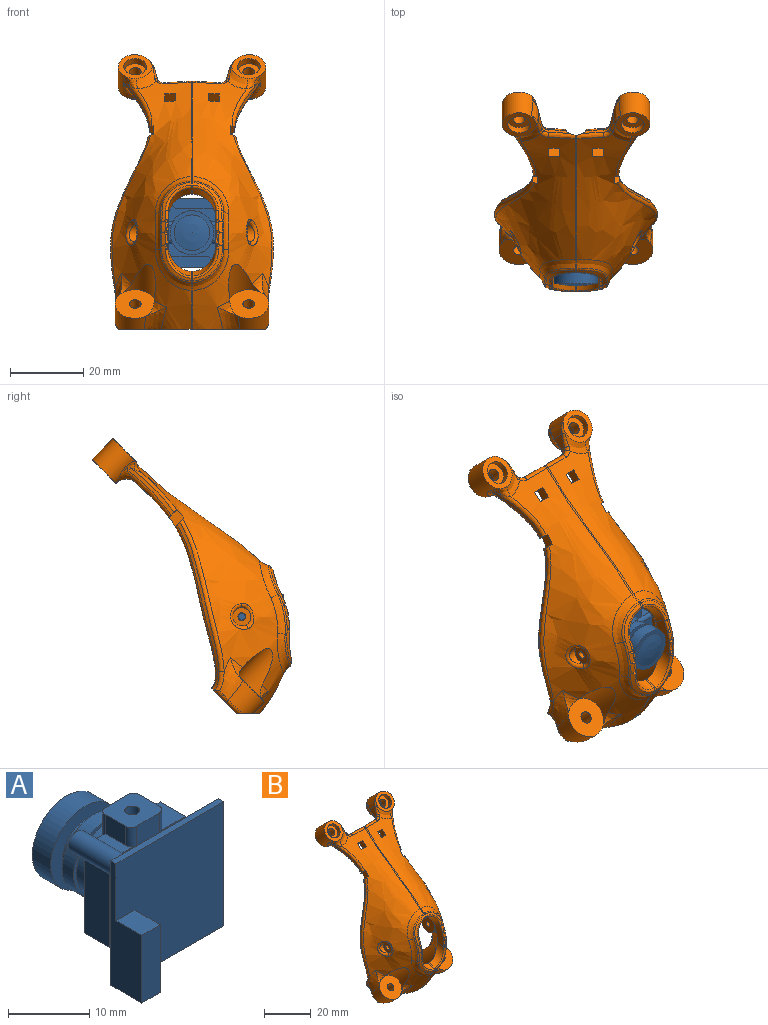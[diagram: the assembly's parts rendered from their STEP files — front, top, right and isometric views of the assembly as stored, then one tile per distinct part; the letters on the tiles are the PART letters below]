
ASSEMBLY  parts=2 mates=1
PART A: 64 faces, bbox 18.8x23x19 mm
  f0: plane 4.4x4.16mm, normal (0,0,-1), area 16mm2, adj f2,f4,f24,f46,f50
  f1: plane 4.4x2.04mm, normal (0,0,1), area 6.7mm2, adj f2,f4,f27,f55,f56
  f2: plane 16x6.4mm, normal (0,1,0), area 36.7mm2, adj f0,f1,f6,f24,f25,f26,f27,f44
  f3: plane 16x6.4mm, normal (0,1,0), area 36.7mm2, adj f7,f19,f20,f21,f22,f23,f28,f43
  f4: plane 15.56x6.52mm, normal (0,-1,0), area 33.6mm2, adj f0,f1,f24,f25,f26,f27,f30,f31
  f5: plane 15.56x6.52mm, normal (0,-1,0), area 33.6mm2, adj f19,f20,f21,f22,f23,f28,f29,f30
  f6: torus R=6mm, axis (0,1,0), area 17mm2, adj f2,f34,f44,f52
  f7: torus R=6mm, axis (0,1,0), area 17mm2, adj f3,f34,f43,f53
  f8: plane 1.5x1.5mm, normal (0,1,0), area 0.5mm2, adj f13,f14,f26
  f9: plane 18.8x18.8mm, normal (0,1,0), area 238.3mm2, adj f12,f13,f14,f15,f21,f26,f29,f30
  f10: plane 1.5x1.5mm, normal (0,1,0), area 0.5mm2, adj f12,f15,f21
  f11: plane 18.8x18.8mm, normal (0,-1,0), area 320.3mm2, adj f12,f13,f14,f15,f16,f17
  f12: plane 18.8x0.9mm, normal (1,0,0), area 16.9mm2, adj f9,f10,f11,f13,f15
  f13: plane 18.8x0.9mm, normal (0,0,1), area 16.9mm2, adj f8,f9,f11,f12,f14
  f14: plane 18.8x5.4mm, normal (-1,0,0), area 62.8mm2, adj f8,f9,f11,f13,f15,f16,f18
  f15: plane 18.8x5.4mm, normal (0,0,-1), area 31.5mm2, adj f9,f10,f11,f12,f14,f17,f18
  f16: plane 4.5x3.25mm, normal (0,0,1), area 14.6mm2, adj f11,f14,f17,f18
  f17: plane 10.2x4.5mm, normal (1,0,0), area 45.9mm2, adj f11,f15,f16,f18
  f18: plane 10.2x3.25mm, normal (0,-1,0), area 33.1mm2, adj f14,f15,f16,f17
  f19: plane 11.08x4.4mm, normal (1,0,0), area 48.7mm2, adj f3,f5,f20,f28
  f20: plane 4.4x2.36mm, normal (0.71,0,0.71), area 14.7mm2, adj f3,f5,f19,f21
  f21: cylinder r=1.5mm len=7.4mm, axis (0,-1,0), area 49mm2, adj f3,f5,f9,f10,f20,f22
  f22: plane 4.4x2.36mm, normal (-0.71,0,-0.71), area 14.7mm2, adj f3,f5,f21,f23
  f23: plane 4.4x2.04mm, normal (0,0,-1), area 6.7mm2, adj f3,f5,f22,f47,f49
  f24: plane 11.08x4.4mm, normal (-1,0,0), area 48.7mm2, adj f0,f2,f4,f25
  f25: plane 4.4x2.36mm, normal (-0.71,0,-0.71), area 14.7mm2, adj f2,f4,f24,f26
  f26: cylinder r=1.5mm len=7.4mm, axis (0,-1,0), area 49mm2, adj f2,f4,f8,f9,f25,f27
  f27: plane 4.4x2.36mm, normal (0.71,0,0.71), area 14.7mm2, adj f1,f2,f4,f26
  f28: plane 4.4x4.16mm, normal (0,0,1), area 16mm2, adj f3,f5,f19,f57,f58
  f29: plane 10x3mm, normal (1,0,0), area 30mm2, adj f5,f9,f30,f32
  f30: plane 10x3mm, normal (0,0,1), area 29.5mm2, adj f4,f5,f9,f29,f31,f51,f56,f57
  f31: plane 10x3mm, normal (-1,0,0), area 30mm2, adj f4,f9,f30,f32
  f32: plane 10x3mm, normal (0,0,-1), area 29.5mm2, adj f4,f5,f9,f29,f31,f46,f47,f48
  f33: plane 11x11mm, normal (0,-1,0), area 16.5mm2, adj f34,f41
  f34: cylinder r=5mm len=10mm, axis (0,-1,0), area 62.8mm2, adj f6,f7,f33,f45,f54
  f35: sphere r=23.77mm, area 74.7mm2, adj f36
  f36: plane 12x12mm, normal (0,1,0), area 39.2mm2, adj f35,f37
  f37: cylinder r=6mm len=12mm, axis (0,-1,0), area 120.6mm2, adj f36,f38
  f38: plane 12x12mm, normal (0,-1,0), area 65.3mm2, adj f37,f39
  f39: cylinder r=3.9mm len=7.8mm, axis (0,-1,0), area 36.8mm2, adj f38,f40
  f40: plane 11x11mm, normal (0,1,0), area 47.2mm2, adj f39,f41
  f41: cylinder r=5.5mm len=11mm, axis (0,-1,0), area 69.1mm2, adj f33,f40
  f42: plane 6x5.5mm, normal (0,0,-1), area 29.5mm2, adj f43,f44,f45,f46,f47,f48,f49,f50
  f43: cylinder r=1mm len=5.26mm, axis (0,0,-1), area 8mm2, adj f3,f7,f42,f45,f49
  f44: cylinder r=1mm len=5.26mm, axis (0,0,-1), area 8mm2, adj f2,f6,f42,f45,f50
  f45: plane 4.92x4mm, normal (0,1,0), area 18.5mm2, adj f34,f42,f43,f44
  f46: cylinder r=1mm len=4.5mm, axis (0,0,-1), area 5.3mm2, adj f0,f4,f32,f42,f48,f50
  f47: cylinder r=1mm len=4.5mm, axis (0,0,-1), area 5.3mm2, adj f5,f23,f32,f42,f48,f49
  f48: plane 4.5x4mm, normal (0,-1,0), area 18mm2, adj f32,f42,f46,f47
  f49: plane 3.5x2.9mm, normal (1,0,0), area 10.1mm2, adj f23,f42,f43,f47
  f50: plane 3.5x2.9mm, normal (-1,0,0), area 10.1mm2, adj f0,f42,f44,f46
  f51: plane 4.5x4mm, normal (0,-1,0), area 18mm2, adj f30,f56,f57,f59
  f52: cylinder r=1mm len=5.26mm, axis (0,0,-1), area 8mm2, adj f2,f6,f54,f55,f59
  f53: cylinder r=1mm len=5.26mm, axis (0,0,-1), area 8mm2, adj f3,f7,f54,f58,f59
  f54: plane 4.92x4mm, normal (0,1,0), area 18.5mm2, adj f34,f52,f53,f59
  f55: plane 3.5x2.9mm, normal (-1,0,0), area 10.1mm2, adj f1,f52,f56,f59
  f56: cylinder r=1mm len=4.5mm, axis (0,0,-1), area 5.3mm2, adj f1,f4,f30,f51,f55,f59
  f57: cylinder r=1mm len=4.5mm, axis (0,0,-1), area 5.3mm2, adj f5,f28,f30,f51,f58,f59
  f58: plane 3.5x2.9mm, normal (1,0,0), area 10.1mm2, adj f28,f53,f57,f59
  f59: plane 6x5.5mm, normal (0,0,1), area 29.5mm2, adj f51,f52,f53,f54,f55,f56,f57,f58
  f60: cylinder r=0.92mm len=3mm, axis (0,0,1), area 17.4mm2, adj f59,f61
  f61: plane 1.84x1.84mm, normal (0,0,1), area 2.7mm2, adj f60
  f62: cylinder r=0.92mm len=3mm, axis (0,0,-1), area 17.4mm2, adj f42,f63
  f63: plane 1.84x1.84mm, normal (0,0,-1), area 2.7mm2, adj f62
PART B: 207 faces, bbox 59.9x69.7x87.1 mm
  f0: offset ~83.38x64.32mm, area 1166.9mm2, adj f1,f179,f180,f181,f182,f183,f184,f185
  f1: plane 42.73x8.82mm, normal (0,0,-1), area 150.5mm2, adj f0,f2,f150,f151,f152,f153,f154,f155
  f2: offset ~83.38x64.32mm, area 1167mm2, adj f1,f3,f110,f111,f112,f113,f114,f115
  f3: cylinder r=6.5mm len=9.06mm, axis (0,0.94,0.34), area 37.8mm2, adj f2,f4,f109,f110
  f4: bspline ~9.45x7.43mm, area 9.7mm2, adj f3,f5,f104,f108
  f5: extruded ~0.61x0.5mm, area 0.4mm2, adj f4,f6,f103,f109
  f6: bspline ~9.45x7.43mm, area 9.7mm2, adj f5,f7,f102,f180
  f7: bspline ~10.3x1.54mm, area 3.8mm2, adj f6,f8,f99,f100,f101,f102,f181
  f8: plane 1.49x0.57mm, normal (0,-0.59,0.81), area 0.7mm2, adj f7,f9,f102
  f9: plane 1.49x0.57mm, normal (0,-0.81,-0.59), area 0.7mm2, adj f8,f10,f102,f181
  f10: bspline ~11.99x4.7mm, area 5.6mm2, adj f9,f11,f12,f98,f102,f181
  f11: plane 1.51x0.63mm, normal (0,-0.46,0.89), area 0.7mm2, adj f10,f98,f102
  f12: bspline ~8.27x7.22mm, area 9.9mm2, adj f10,f13,f102,f182
  f13: extruded ~0.76x0.5mm, area 0.4mm2, adj f12,f14,f15,f21
  f14: plane 3x1.73mm, normal (0,-0.5,-0.87), area 1.7mm2, adj f13,f111,f182,f183
  f15: bspline ~8.27x7.22mm, area 9.9mm2, adj f13,f16,f104,f111
  f16: bspline ~11.99x4.7mm, area 5.6mm2, adj f15,f17,f19,f20,f104,f110
  f17: plane 1.49x0.57mm, normal (0,-0.81,-0.59), area 0.7mm2, adj f16,f18,f104,f110
  f18: plane 1.49x0.57mm, normal (0,-0.59,0.81), area 0.7mm2, adj f17,f104,f108
  f19: plane 1.51x0.63mm, normal (0,-0.46,0.89), area 0.7mm2, adj f16,f20,f104
  f20: plane 1.67x0.79mm, normal (0,-0.89,-0.46), area 0.7mm2, adj f16,f19,f104
  f21: extruded ~0.72x0.64mm, area 0.5mm2, adj f13,f22,f102,f104
  f22: extruded ~0.53x0.5mm, area 0.3mm2, adj f21,f23,f36,f37
  f23: bspline ~9x8.93mm, area 8.2mm2, adj f22,f24,f35,f102
  f24: bspline ~12.77x3.71mm, area 7.4mm2, adj f23,f25,f34,f102
  f25: bspline ~13.31x4.39mm, area 27.1mm2, adj f24,f26,f35,f157
  f26: bspline ~12.1x10.04mm, area 39.7mm2, adj f25,f27,f34,f157
  f27: extruded ~2.12x1.67mm, area 1.4mm2, adj f26,f28,f33,f156
  f28: extruded ~0.5x0.5mm, area 0.3mm2, adj f27,f29,f34,f103
  f29: bspline ~9.63x8.97mm, area 8.6mm2, adj f28,f30,f33,f104
  f30: bspline ~12.77x3.71mm, area 7.4mm2, adj f29,f31,f36,f104
  f31: bspline ~12.73x4.11mm, area 27.1mm2, adj f30,f32,f33,f155
  f32: bspline ~10.71x10.27mm, area 38.5mm2, adj f31,f36,f37,f155
  f33: bspline ~12.1x10.04mm, area 39.7mm2, adj f27,f29,f31,f155
  f34: bspline ~9.63x8.97mm, area 8.4mm2, adj f24,f26,f28,f102
  f35: bspline ~10.71x10.27mm, area 38.5mm2, adj f23,f25,f37,f157
  f36: bspline ~8.35x8.01mm, area 8.2mm2, adj f22,f30,f32,f104
  f37: extruded ~2.41x1.29mm, area 1.4mm2, adj f22,f32,f35,f38
  f38: extruded ~32.91x25.65mm, area 20.9mm2, adj f37,f39,f155,f157
  f39: extruded ~0.98x0.5mm, area 0.5mm2, adj f38,f40,f69,f184
  f40: bspline ~10.47x1.89mm, area 11mm2, adj f39,f41,f68,f155,f184
  f41: bspline ~3.3x2.27mm, area 3.1mm2, adj f40,f42,f67,f155
  f42: bspline ~2.19x1.76mm, area 1.6mm2, adj f41,f43,f66,f67
  f43: bspline ~7.53x7.29mm, area 20.4mm2, adj f42,f44,f64,f65,f66,f155
  f44: plane 9.76x7.06mm, normal (0,-0.71,0.71), area 36.3mm2, adj f43,f45,f63,f64
  f45: cylinder r=4.6mm len=12.16mm, axis (0,-0.71,0.71), area 126.1mm2, adj f44,f46,f50,f51,f54,f55,f57,f65
  f46: bspline ~4.8x1.98mm, area 1.7mm2, adj f45,f47,f50,f114
  f47: bspline ~5.53x3.03mm, area 3.6mm2, adj f46,f48,f49,f114
  f48: plane 4.9x4.27mm, normal (0.97,0.17,0.17), area 10.7mm2, adj f47,f50,f66,f67
  f49: bspline ~2.17x2.01mm, area 2.4mm2, adj f47,f67,f113,f114
  f50: bspline ~12.24x12.21mm, area 18.4mm2, adj f45,f46,f48,f65
  f51: bspline ~3.69x2.64mm, area 2.7mm2, adj f45,f52,f54,f64
  f52: bspline ~14.88x14.31mm, area 22.8mm2, adj f51,f53,f64,f117,f155
  f53: bspline ~18.99x18.39mm, area 18.4mm2, adj f52,f54,f116,f117
  f54: bspline ~2.6x2.59mm, area 1.6mm2, adj f45,f51,f53,f55
  f55: bspline ~5.53x4.68mm, area 15.9mm2, adj f45,f54,f56,f116
  f56: bspline ~5.45x1.15mm, area 0.1mm2, adj f55,f57,f115,f116
  f57: plane 9.2x6.51mm, normal (0,0.71,-0.71), area 36.3mm2, adj f45,f56,f58,f115
  f58: cone r=3.1mm half-angle=45deg, axis (0,0.71,-0.71), area 12.7mm2, adj f57,f59
  f59: cylinder r=2.6mm len=5.44mm, axis (0,-0.71,0.71), area 40.8mm2, adj f58,f60
  f60: plane 5.2x3.68mm, normal (0,0.71,-0.71), area 13.2mm2, adj f59,f61
  f61: cylinder r=1.6mm len=4.38mm, axis (0,0.71,-0.71), area 30.2mm2, adj f60,f62
  f62: plane 6.2x4.38mm, normal (0,-0.71,0.71), area 22.1mm2, adj f61,f63
  f63: cylinder r=3.1mm len=6.2mm, axis (0,0.71,-0.71), area 39mm2, adj f44,f62
  f64: bspline ~3.57x3.48mm, area 6.6mm2, adj f43,f44,f51,f52
  f65: bspline ~3.55x2.96mm, area 2.2mm2, adj f43,f45,f50,f66
  f66: bspline ~5.31x4.18mm, area 4.5mm2, adj f42,f43,f48,f65
  f67: cylinder r=2mm len=2.27mm, axis (0,0.71,-0.71), area 3.1mm2, adj f41,f42,f48,f49,f68,f113
  f68: plane 5.67x1.03mm, normal (0,0.71,0.71), area 5.1mm2, adj f40,f67,f112,f184
  f69: bspline ~10.47x1.89mm, area 11mm2, adj f39,f70,f97,f157,f184
  f70: bspline ~3.3x2.27mm, area 3.1mm2, adj f69,f71,f96,f157
  f71: cylinder r=2mm len=2.27mm, axis (0,0.71,-0.71), area 3.1mm2, adj f70,f72,f95,f96,f97,f186
  f72: plane 4.9x4.27mm, normal (-0.97,0.17,0.17), area 10.7mm2, adj f71,f73,f93,f94
  f73: bspline ~5.53x3.03mm, area 3.6mm2, adj f72,f74,f95,f187
  f74: bspline ~4.8x1.98mm, area 1.7mm2, adj f73,f75,f93,f187
  f75: cylinder r=4.6mm len=12.16mm, axis (0,-0.71,0.71), area 126.1mm2, adj f74,f76,f84,f85,f90,f91,f92,f93
  f76: plane 9.2x6.51mm, normal (0,0.71,-0.71), area 36.3mm2, adj f75,f77,f78,f188
  f77: bspline ~5.45x1.15mm, area 0.1mm2, adj f76,f84,f188,f189
  f78: cone r=3.1mm half-angle=45deg, axis (0,0.71,-0.71), area 12.7mm2, adj f76,f79
  f79: cylinder r=2.6mm len=5.44mm, axis (0,-0.71,0.71), area 40.8mm2, adj f78,f80
  f80: plane 5.2x3.68mm, normal (0,0.71,-0.71), area 13.2mm2, adj f79,f81
  f81: cylinder r=1.6mm len=4.38mm, axis (0,0.71,-0.71), area 30.2mm2, adj f80,f82
  f82: plane 6.2x4.38mm, normal (0,-0.71,0.71), area 22.1mm2, adj f81,f83
  f83: cylinder r=3.1mm len=6.2mm, axis (0,0.71,-0.71), area 39mm2, adj f82,f91
  f84: bspline ~5.52x5mm, area 16.5mm2, adj f75,f77,f85,f189
  f85: bspline ~2.6x2.59mm, area 1.6mm2, adj f75,f84,f86,f90
  f86: bspline ~18.99x18.39mm, area 18.4mm2, adj f85,f87,f189,f190
  f87: bspline ~14.88x14.31mm, area 22.8mm2, adj f86,f88,f90,f157,f190
  f88: bspline ~3.57x3.48mm, area 6.6mm2, adj f87,f89,f90,f91
  f89: bspline ~7.53x7.29mm, area 20.4mm2, adj f88,f91,f92,f94,f96,f157
  f90: bspline ~3.09x2.06mm, area 2.7mm2, adj f75,f85,f87,f88
  f91: plane 9.76x7.06mm, normal (0,-0.71,0.71), area 36.3mm2, adj f75,f83,f88,f89
  f92: bspline ~3.55x2.96mm, area 2.2mm2, adj f75,f89,f93,f94
  f93: bspline ~12.24x12.21mm, area 18.4mm2, adj f72,f74,f75,f92
  f94: bspline ~5.31x4.18mm, area 4.5mm2, adj f72,f89,f92,f96
  f95: bspline ~2.17x2.01mm, area 2.4mm2, adj f71,f73,f186,f187
  f96: bspline ~2.19x1.76mm, area 1.6mm2, adj f70,f71,f89,f94
  f97: plane 5.67x1.03mm, normal (0,0.71,0.71), area 5.1mm2, adj f69,f71,f184,f185
  f98: plane 1.67x0.79mm, normal (0,-0.89,-0.46), area 0.7mm2, adj f10,f11,f102
  f99: plane 1.63x0.66mm, normal (0,-0.71,-0.71), area 0.7mm2, adj f7,f100,f101,f102
  f100: extruded ~0.99x0.02mm, area 0mm2, adj f7,f99,f101
  f101: plane 1.63x0.66mm, normal (0,-0.71,0.71), area 0.7mm2, adj f7,f99,f100,f102
  f102: offset ~73.93x54.26mm, area 38.2mm2, adj f6,f7,f8,f9,f10,f11,f12,f21
  f103: extruded ~0.72x0.5mm, area 0.4mm2, adj f5,f28,f102,f104
  f104: offset ~73.93x54.26mm, area 38.2mm2, adj f4,f15,f16,f17,f18,f19,f20,f21
  f105: plane 1.63x0.66mm, normal (0,-0.71,0.71), area 0.7mm2, adj f104,f106,f107,f108
  f106: extruded ~0.99x0.02mm, area 0mm2, adj f105,f107,f108
  f107: plane 1.63x0.66mm, normal (0,-0.71,-0.71), area 0.7mm2, adj f104,f105,f106,f108
  f108: bspline ~10.3x1.54mm, area 3.8mm2, adj f4,f18,f104,f105,f106,f107,f110
  f109: plane 3.33x1.21mm, normal (0,-0.34,0.94), area 1.8mm2, adj f3,f5,f179,f180
  f110: plane 10.55x5.43mm, normal (1,0,0), area 34.9mm2, adj f2,f3,f16,f17,f108,f111
  f111: cylinder r=6.5mm len=8.13mm, axis (0,0.87,-0.5), area 36mm2, adj f2,f14,f15,f110
  f112: bspline ~7.44x1.8mm, area 7.2mm2, adj f2,f68,f113,f184
  f113: bspline ~2.84x1.75mm, area 2.1mm2, adj f2,f49,f67,f112
  f114: bspline ~11.02x10.53mm, area 30.6mm2, adj f2,f45,f46,f47,f49,f115
  f115: bspline ~6.13x4.96mm, area 14.6mm2, adj f2,f56,f57,f114
  f116: bspline ~15.96x15.64mm, area 28.1mm2, adj f2,f53,f55,f56,f117
  f117: plane 2.27x2.27mm, normal (0,-0.71,-0.71), area 3.5mm2, adj f2,f52,f53,f116,f119,f155
  f118: bspline ~3.81x2.88mm, area 0mm2, adj f2,f119
  f119: plane 4.78x4.2mm, normal (-1,0,0), area 9.6mm2, adj f2,f117,f118,f120,f155
  f120: plane 2.6x2.6mm, normal (0,0.71,0.71), area 4.4mm2, adj f2,f119,f121,f131,f132,f155
  f121: bspline ~44.48x12.97mm, area 63.5mm2, adj f120,f122,f131,f155
  f122: bspline ~7.25x2.84mm, area 7.9mm2, adj f121,f123,f130,f131,f151
  f123: bspline ~13.39x11.03mm, area 39.6mm2, adj f122,f124,f128,f129,f130,f153,f155
  f124: plane 11.03x7.81mm, normal (0,-0.71,0.71), area 87.1mm2, adj f123,f125,f127,f128,f153
  f125: cylinder r=5.5mm len=15.27mm, axis (0,0.71,-0.71), area 101.2mm2, adj f124,f126,f128,f154,f155
  f126: bspline ~7.27x6.73mm, area 11.1mm2, adj f125,f154,f155
  f127: cylinder r=1.6mm len=7.53mm, axis (0,0.71,-0.71), area 74.9mm2, adj f124,f151
  f128: bspline ~7.81x7.65mm, area 10.8mm2, adj f123,f124,f125,f155
  f129: bspline ~3.81x3.61mm, area 2.7mm2, adj f123,f130,f151,f152
  f130: bspline ~3.59x3.34mm, area 2.7mm2, adj f122,f123,f129,f151
  f131: bspline ~48.07x13.97mm, area 50.4mm2, adj f120,f121,f122,f132,f151
  f132: bspline ~45.48x12.06mm, area 81mm2, adj f2,f120,f131,f151
  f133: cylinder r=7mm len=15.45mm, axis (0,0.71,-0.71), area 131.2mm2, adj f2,f134
  f134: torus R=6mm, axis (0,-0.71,0.71), area 17.9mm2, adj f2,f133,f150,f151
  f135: bspline ~6.77x3.33mm, area 11.7mm2, adj f2,f136,f143
  f136: plane 8.09x8.09mm, normal (1,0,0), area 46.8mm2, adj f135,f137,f138
  f137: cylinder r=4mm len=8mm, axis (1,0,0), area 56.2mm2, adj f136,f143
  f138: cylinder r=1.05mm len=5.5mm, axis (-1,0,0), area 36.3mm2, adj f136,f139
  f139: plane 5.39x5.39mm, normal (-1,0,0), area 16.2mm2, adj f138,f140,f142
  f140: cylinder r=2.5mm len=4.98mm, axis (-1,0,0), area 0mm2, adj f139,f141
  f141: bspline ~7.14x4.82mm, area 14.7mm2, adj f140,f142,f155
  f142: bspline ~6.99x3.93mm, area 8.9mm2, adj f139,f141,f155
  f143: bspline ~10.31x9.98mm, area 37.2mm2, adj f2,f135,f137
  f144: plane 3.14x2.42mm, normal (0,0.71,0.71), area 9mm2, adj f2,f145,f147,f155
  f145: plane 4.32x4.22mm, normal (1,0,0), area 9mm2, adj f2,f144,f146,f155
  f146: plane 3.17x2.43mm, normal (0,-0.71,-0.71), area 9mm2, adj f2,f145,f147,f155
  f147: plane 4.36x4.22mm, normal (-1,0,0), area 9mm2, adj f2,f144,f146,f155
  f148: plane 5.99x5.14mm, normal (1,0,0), area 14.4mm2, adj f2,f149
  f149: cylinder r=3.5mm len=5.99mm, axis (1,0,0), area 0mm2, adj f2,f148
  f150: bspline ~6.18x3.51mm, area 2.8mm2, adj f1,f2,f134,f151
  f151: plane 11.84x6.92mm, normal (0,0.71,-0.71), area 78.6mm2, adj f1,f2,f122,f127,f129,f130,f131,f132
  f152: torus R=4.5mm, axis (0,-0.71,0.71), area 5.8mm2, adj f1,f129,f151,f153
  f153: cylinder r=5.5mm len=10.45mm, axis (0,0.71,-0.71), area 82.9mm2, adj f1,f123,f124,f152,f154
  f154: bspline ~10.34x9.11mm, area 31.9mm2, adj f1,f125,f126,f153,f155
  f155: bspline ~77.07x58.32mm, area 1188.6mm2, adj f1,f31,f32,f33,f38,f40,f41,f43
  f156: extruded ~10.63x6.39mm, area 6.2mm2, adj f1,f27,f155,f157
  f157: bspline ~77.07x58.32mm, area 1188.6mm2, adj f1,f25,f26,f35,f38,f69,f70,f87
  f158: bspline ~43.59x12.97mm, area 63.5mm2, adj f157,f159,f160,f193
  f159: bspline ~48.07x13.97mm, area 50.4mm2, adj f158,f160,f193,f194,f195
  f160: bspline ~7.25x2.84mm, area 7.9mm2, adj f158,f159,f161,f163,f195
  f161: bspline ~3.59x3.34mm, area 2.7mm2, adj f160,f162,f163,f195
  f162: bspline ~3.81x3.61mm, area 2.7mm2, adj f161,f163,f178,f195
  f163: bspline ~13.07x10.82mm, area 39.6mm2, adj f157,f160,f161,f162,f164,f166,f177
  f164: plane 11.03x7.81mm, normal (0,-0.71,0.71), area 87.1mm2, adj f163,f165,f166,f167,f177
  f165: cylinder r=1.6mm len=7.53mm, axis (0,0.71,-0.71), area 74.9mm2, adj f164,f195
  f166: bspline ~7.81x7.65mm, area 10.8mm2, adj f157,f163,f164,f167
  f167: cylinder r=5.5mm len=15.27mm, axis (0,0.71,-0.71), area 101.2mm2, adj f157,f164,f166,f168,f176
  f168: bspline ~7.27x6.73mm, area 11.1mm2, adj f157,f167,f176
  f169: bspline ~7.14x4.82mm, area 14.7mm2, adj f157,f170,f175
  f170: cylinder r=2.5mm len=4.98mm, axis (1,0,0), area 0mm2, adj f169,f171
  f171: plane 5.39x5.39mm, normal (1,0,0), area 16.2mm2, adj f170,f172,f175
  f172: cylinder r=1.05mm len=5.5mm, axis (1,0,0), area 36.3mm2, adj f171,f173
  f173: plane 8.09x8.09mm, normal (-1,0,0), area 46.8mm2, adj f172,f174,f200
  f174: cylinder r=4mm len=8mm, axis (-1,0,0), area 56.2mm2, adj f173,f199
  f175: bspline ~6.99x3.93mm, area 8.9mm2, adj f157,f169,f171
  f176: bspline ~10.34x9.11mm, area 31.9mm2, adj f1,f157,f167,f168,f177
  f177: cylinder r=5.5mm len=10.45mm, axis (0,0.71,-0.71), area 82.9mm2, adj f1,f163,f164,f176,f178
  f178: torus R=4.5mm, axis (0,-0.71,0.71), area 5.8mm2, adj f1,f162,f177,f195
  f179: extruded ~15.8x8.98mm, area 9.1mm2, adj f0,f1,f2,f109
  f180: cylinder r=6.5mm len=9.06mm, axis (0,0.94,0.34), area 37.8mm2, adj f0,f6,f109,f181
  f181: plane 10.55x5.43mm, normal (-1,0,0), area 34.9mm2, adj f0,f7,f9,f10,f180,f182
  f182: cylinder r=6.5mm len=8.13mm, axis (0,0.87,-0.5), area 36mm2, adj f0,f12,f14,f181
  f183: extruded ~27.76x21.32mm, area 17.5mm2, adj f0,f2,f14,f184
  f184: cylinder r=3mm len=10.86mm, axis (0,0.57,0.82), area 70mm2, adj f0,f2,f39,f40,f68,f69,f97,f112
  f185: bspline ~7.44x1.8mm, area 7.2mm2, adj f0,f97,f184,f186
  f186: bspline ~2.84x1.75mm, area 2.1mm2, adj f0,f71,f95,f185
  f187: bspline ~10.96x10.5mm, area 30.6mm2, adj f0,f73,f74,f75,f95,f188
  f188: bspline ~6.13x4.96mm, area 14.6mm2, adj f0,f76,f77,f187
  f189: bspline ~14.59x14.53mm, area 28.1mm2, adj f0,f77,f84,f86,f190
  f190: plane 2.27x2.27mm, normal (0,-0.71,-0.71), area 3.5mm2, adj f0,f86,f87,f157,f189,f192
  f191: bspline ~3.81x2.88mm, area 0mm2, adj f0,f192
  f192: plane 4.78x4.2mm, normal (1,0,0), area 9.6mm2, adj f0,f157,f190,f191,f193
  f193: plane 2.6x2.6mm, normal (0,0.71,0.71), area 4.4mm2, adj f0,f157,f158,f159,f192,f194
  f194: bspline ~45.48x12.06mm, area 81mm2, adj f0,f159,f193,f195
  f195: plane 11.84x6.92mm, normal (0,0.71,-0.71), area 78.6mm2, adj f0,f1,f159,f160,f161,f162,f165,f178
  f196: cylinder r=7mm len=15.45mm, axis (0,0.71,-0.71), area 131.3mm2, adj f0,f197
  f197: torus R=6mm, axis (0,-0.71,0.71), area 17.9mm2, adj f0,f195,f196,f198
  f198: bspline ~6.18x3.51mm, area 2.8mm2, adj f0,f1,f195,f197
  f199: bspline ~10.31x9.72mm, area 37.2mm2, adj f0,f174,f200
  f200: bspline ~6.77x3.33mm, area 11.7mm2, adj f0,f173,f199
  f201: plane 4.36x4.22mm, normal (1,0,0), area 9mm2, adj f0,f157,f202,f204
  f202: plane 3.14x2.42mm, normal (0,0.71,0.71), area 9mm2, adj f0,f157,f201,f203
  f203: plane 4.32x4.22mm, normal (-1,0,0), area 9mm2, adj f0,f157,f202,f204
  f204: plane 3.17x2.43mm, normal (0,-0.71,-0.71), area 9mm2, adj f0,f157,f201,f203
  f205: cylinder r=3.5mm len=5.99mm, axis (-1,0,0), area 0mm2, adj f0,f206
  f206: plane 5.99x5.14mm, normal (-1,0,0), area 14.4mm2, adj f0,f205
PLACE A rot(axis=(0.71,0,-0.71),180deg) t=(0,-7,9.4)mm
PLACE B rot(axis=(1,0,0),0.1deg) t=(0,-21.89,-10.25)mm
MATE revolute A.f60 <-> B.f137  axis (1,0,0) through (9.5,-6.55,9.4)mm
